# Revit family: Regadera H-3011
name_source: partatom
category: Aparatos sanitarios
revit_build: Autodesk Revit 2016 (Build: 20150220_1215(x64)
units: mm (PartAtom-declared; Revit-internal decimal feet)

## family parameters
Compartido = Sí
Corte con vacíos al cargar = No
Cota de conector redondo = Diámetro de uso
Número OmniClass = 23.45.05.14.17
Punto de cálculo de habitación = Sí
Se basa en plano de trabajo = Sí
Siempre vertical = Sí
Tipo de pieza = Normal
Título OmniClass = Showers

## types (1)
- H-3011
    Brass Chromed = Brass
    Comentarios de tipo = Regadera de plato ancho de 12"
    Compliance = NOM-008-CONAGUA-1998
    Descripción = Regadera de Plato Ancho de 12" Corro Fijo con Sistema Anticalcáreo
    Elevación por defecto = 1"
    Fabricante = HELVEX S.A. de C.V.
    Features = Regadera de Plato Ancho de 12" Corro Fijo con Sistema Anticalcáreo
    Imagen de tipo = H-3011.jpg
    Inlet Threads = ½" - 14 NPT
    Max. Water Flow = 2.2 gal/min
    Max. Working Pressure = 85.3 psi
    Min. Working Pressure = 14.2 psi
    Modelo = H-3011
    Total Height = 12"
    Total Length = 2"

## geometry (parser evidence)
native form markers: Sweep x3
no freeform markers — native parametric forms only
